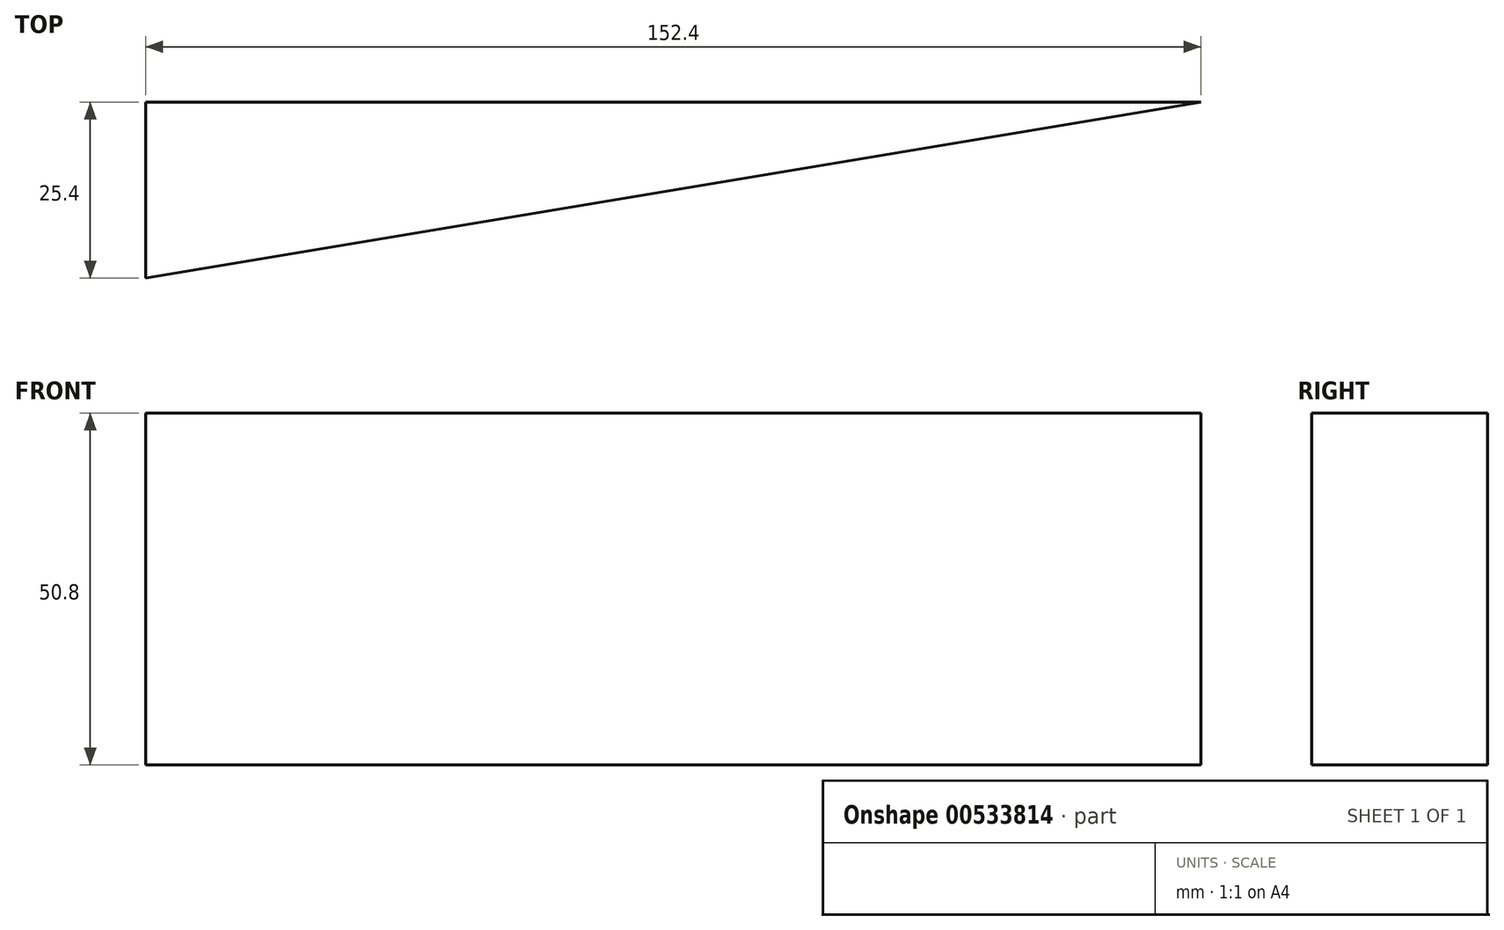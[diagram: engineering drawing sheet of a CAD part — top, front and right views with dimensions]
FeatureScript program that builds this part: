
annotation { "Feature Type Name" : "Feature", "Feature Type Description" : "" }
export const myFeature = defineFeature(function(context is Context, id is Id, definition is map)
    precondition{}
    {
        {
            var Q0;
            Q0=qCreatedBy(makeId("Front.planeOp"),FACE);
            var sketch = newSketch(context, id + "F0", { "sketchPlane" : qUnion([Q0])});
            skLineSegment(sketch, "E0.bottom", {"start": v(-155.52, -85.6) * mm, "end": v(-3.12, -85.6) * mm});
            skLineSegment(sketch, "E0.top", {"start": v(-155.52, -34.8) * mm, "end": v(-3.12, -34.8) * mm});
            skLineSegment(sketch, "E0.left", {"start": v(-155.52, -85.6) * mm, "end": v(-155.52, -34.8) * mm});
            skLineSegment(sketch, "E0.right", {"start": v(-3.12, -85.6) * mm, "end": v(-3.12, -34.8) * mm});
            skSolve(sketch);
        }
        {
            var Q0;
            Q0=makeQuery(id+"F0.imprint","IMPRINT",FACE,{"disambiguationData":[TD([[makeQuery(id+"F0.imprint","IMPRINT",EDGE,{"derivedFrom":sQuery(id+"F0.wireOp",EDGE,"E0.bottom")}),1.0]])]});
            extrude(context, id + "F1", {"entities" : qUnion([Q0]), "depth" : 25.4 * mm, "offsetDistance" : 25.4 * mm});
        }
        {
            var Q0;
            Q0=makeQuery(id+"F1.opExtrude","SWEPT_FACE",FACE,{"disambiguationData":[OSD([sQuery(id+"F0.wireOp",EDGE,"E0.top")])]});
            var sketch = newSketch(context, id + "F2", { "sketchPlane" : qUnion([Q0])});
            skLineSegment(sketch, "E1", {"start": v(-155.52, 0) * mm, "end": v(-3.12, -25.4) * mm});
            skLineSegment(sketch, "E2", {"start": v(-155.52, -25.4) * mm, "end": v(-3.12, 0) * mm});
            skCircle(sketch, "E3", {"center": v(-79.32, -12.7) * mm, "radius": 1.59 * mm});
            skSolve(sketch);
        }
        {
            var Q0;
            {var subQ0=sQuery(id+"F2.wireOp",EDGE,"E2");var subQ1=sQuery(id+"F2.wireOp",EDGE,"E1");var subQ2=makeQuery(id+"F2.imprint","INTERSECT",VERTEX,{"derivedFrom":[subQ1,subQ0]});Q0=makeQuery(id+"F2.imprint","IMPRINT",FACE,{"disambiguationData":[TD([[makeQuery(id+"F2.imprint","IMPRINT",EDGE,{"disambiguationData":[TD([[subQ2,-1.0]])],"derivedFrom":subQ1}),1.0]])]});}
            var Q1;
            {var subQ0=sQuery(id+"F2.wireOp",EDGE,"E3");var subQ1=sQuery(id+"F2.wireOp",EDGE,"E1");var subQ2=makeQuery(id+"F2.imprint","INTERSECT",VERTEX,{"disambiguationData":[OD(0.0)],"derivedFrom":[subQ1,subQ0]});Q1=makeQuery(id+"F2.imprint","IMPRINT",FACE,{"disambiguationData":[TD([[makeQuery(id+"F2.imprint","IMPRINT",EDGE,{"disambiguationData":[TD([[subQ2,-1.0]])],"derivedFrom":subQ1}),1.0]])]});}
            var Q2;
            {var subQ0=sQuery(id+"F2.wireOp",EDGE,"E3");var subQ1=sQuery(id+"F2.wireOp",EDGE,"E1");var subQ2=makeQuery(id+"F2.imprint","INTERSECT",VERTEX,{"disambiguationData":[OD(0.0)],"derivedFrom":[subQ1,subQ0]});Q2=makeQuery(id+"F2.imprint","IMPRINT",FACE,{"disambiguationData":[TD([[makeQuery(id+"F2.imprint","IMPRINT",EDGE,{"disambiguationData":[TD([[subQ2,-1.0]])],"derivedFrom":subQ1}),-1.0]])]});}
            var Q3;
            {var subQ0=sQuery(id+"F2.wireOp",EDGE,"E2");var subQ1=sQuery(id+"F2.wireOp",EDGE,"E1");var subQ2=makeQuery(id+"F2.imprint","INTERSECT",VERTEX,{"derivedFrom":[subQ1,subQ0]});Q3=makeQuery(id+"F2.imprint","IMPRINT",FACE,{"disambiguationData":[TD([[makeQuery(id+"F2.imprint","IMPRINT",EDGE,{"disambiguationData":[TD([[subQ2,-1.0]])],"derivedFrom":subQ1}),-1.0]])]});}
            extrude(context, id + "F3", {"entities" : qUnion([Q0, Q1, Q2, Q3]), "operationType" : NewBodyOperationType.REMOVE, "oppositeDirection" : true, "depth" : 50.8 * mm, "offsetDistance" : 25.4 * mm});
        }
    });
